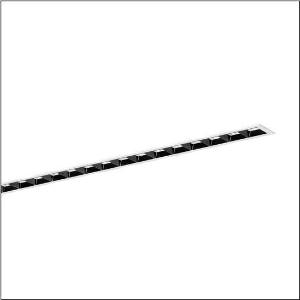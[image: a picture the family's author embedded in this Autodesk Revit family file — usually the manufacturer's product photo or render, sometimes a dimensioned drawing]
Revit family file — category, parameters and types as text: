
# Revit family: silica_21_51mx14tctaw
name_source: partatom
category: Lighting Fixtures
units: mm (PartAtom-declared; Revit-internal decimal feet)

## family parameters
Cut with Voids When Loaded = No
Host = Face
Light Source = No
Part Type = Normal
Room Calculation Point = No
Round Connector Dimension = Use Diameter
Shared = No

## types (1)
- --- (1 x LED, 8200 lm, 81.1 W, 6500K)
    Apparent Load = 81 VA
    CIE Flux Codes = 74 94 99 100 100
    Color Rendering = 80
    Color Temperature = 6500K
    Default Elevation = 1800 mm
    Description = Silica 21, office luminaire, primary light control with darklight reflector, of PMMA, black, light emission: direct distribution, primary light characteristic: asymmetric, installation type: recessed, LED, rated luminous flux: 8.200lm, luminous efficacy: 96lm/W, light colour: 8tw, colour temperature: 2700..6500K, control gear: DALI DT8, with terminal, 3+2-pole, max. 2.5mm², mains connection: 220..240V, AC, 50/60Hz, rated input power: 85.2W, luminaire housing, of aluminium, traffic white (RAL 9016), length: 3.028mm, width: 79mm, height: 53mm, protection rating (complete): IP20, insulation class (complete): insulation class I (protective earthing), certification: CE, ENEC, VDE, permissible operating ambient temperature: 0..+35°C, standard: EN 50419, packaging unit: 1 piece
    Height = 0 mm  [stored 0 ft]
    Lamp = 1 x LED
    Lamp Light Flux = 8200 lm
    Lamp Power = 81.1 W
    Lamp count = 1
    Length = 3027 mm
    Luminous efficacy = 101 lm/W
    Manufacturer = Siteco
    ModVariant = No
    Model = 51MX14TCTAW
    Mounting Place = Ceiling
    Mounting Type = Recessed
    Number of Poles = 1
    OnlyDefault = Yes
    Power Factor = 1
    Product Name = Silica 21
    Product group = office luminaire | ceiling recessed
    ProductGroupID = 400
    Protection Class = Protection class I
    Protection Degree = IP 20
    RLX_Detail_Level = 1
    RLX_Emergency_Light_Flux = 0 lm
    RLX_Emergency_Type = 0
    RLX_Emergency_Type_DB = No
    RlxData = <blob elided: 60329 chars, md5=0051b8b5>
    Socket = socket
    Standby Power = 0 W
    System Light Flux = 8200 lm
    System Power = 81 W
    Type Comments = individual setting
    Type Image = l_1335880.jpg
    URL = http://relux.com
    VarID = @adj_141073
    Voltage = 0 V
    Weight = 0.00 kg
    Width = 79 mm

note: [stored X ft] marks values corroborated as IEEE doubles in the binary element streams (Revit-internal decimal feet)

## geometry (parser evidence)
native form markers: Blend x4, Sweep x12
no freeform markers — native parametric forms only
